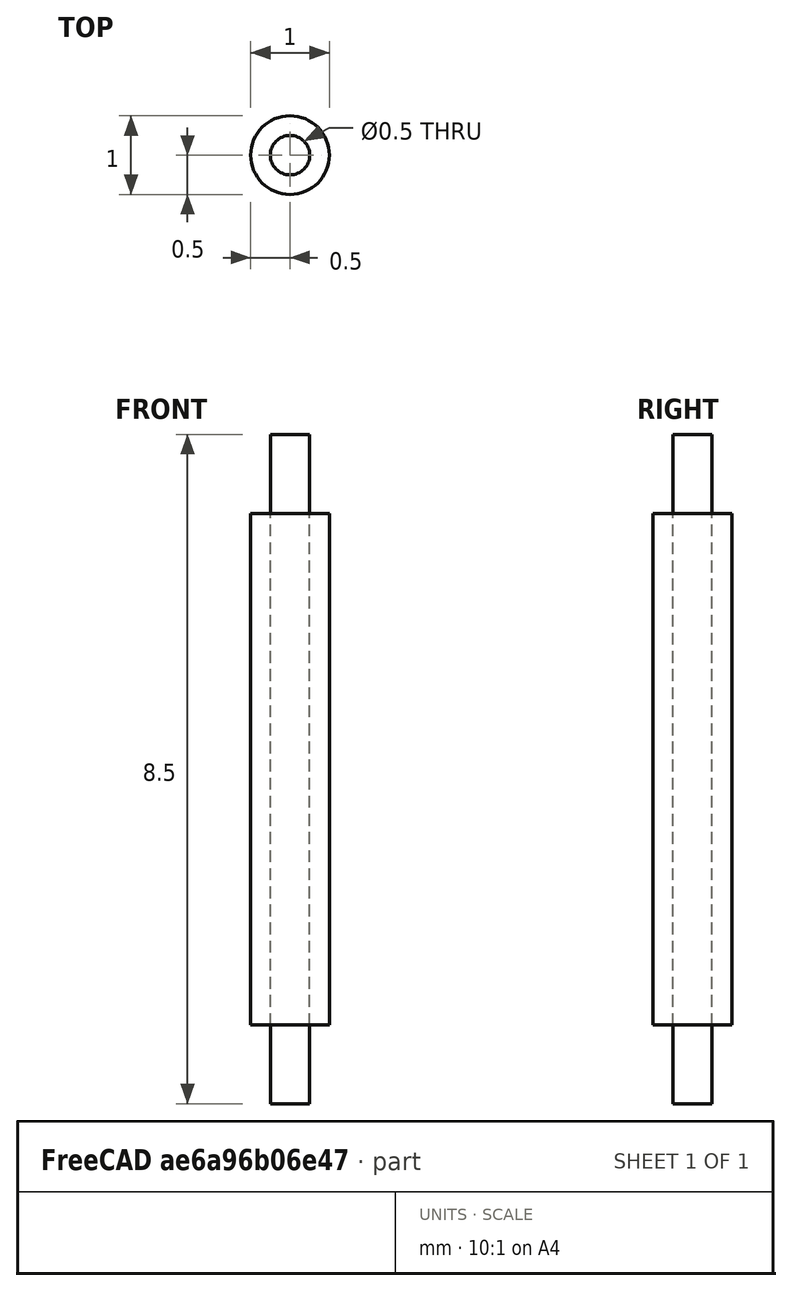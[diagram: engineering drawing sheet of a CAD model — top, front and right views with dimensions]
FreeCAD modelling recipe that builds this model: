
FCSTD DOCUMENT  (FreeCAD 0.19R24291 (Git))
Label: coil_pins02
License: All rights reserved
LicenseURL: http://en.wikipedia.org/wiki/All_rights_reserved
objects: Spreadsheet::Sheet×1, PartDesign::Body×1, Part::FeaturePython×1, Part::Cylinder×1
note: 3 computed .brp shape members not serialized (recipe doc carries the construction recipe); baked Part::Feature solids carry a one-line shape summary decoded from their .brp

FEATURE [Spreadsheet::Sheet] Spreadsheet
  cells = A2=coil pins; B2=rad; C2(pin_r)=0.5; D2(pin_wr)=0.25; B3=rad ins; C3(pin_ri)=0.25; B4=ln; C4(pin_ln)=6.5; D4(pin_wln)=8.5
FEATURE [PartDesign::Body] Body
  Origin = -> Origin
FEATURE [Part::FeaturePython] Tube  # WARN: FeaturePython — macro-defined, semantics opaque (R4)
  AttacherType = Attacher::AttachEngine3D
  Height = 6.5
  InnerRadius = 0.25
  OuterRadius = 0.5
  expr: OuterRadius = Spreadsheet.pin_r
  expr: InnerRadius = Spreadsheet.pin_ri
  expr: Height = Spreadsheet.pin_ln
FEATURE [Part::Cylinder] Cylinder
  Angle = 360
  AttacherType = Attacher::AttachEngine3D
  Height = 8.5
  Placement = pos=(0,0,-1) rot=(0,0,1;0rad)
  Radius = 0.25
  expr: Radius = Spreadsheet.pin_wr
  expr: Height = Spreadsheet.pin_wln
